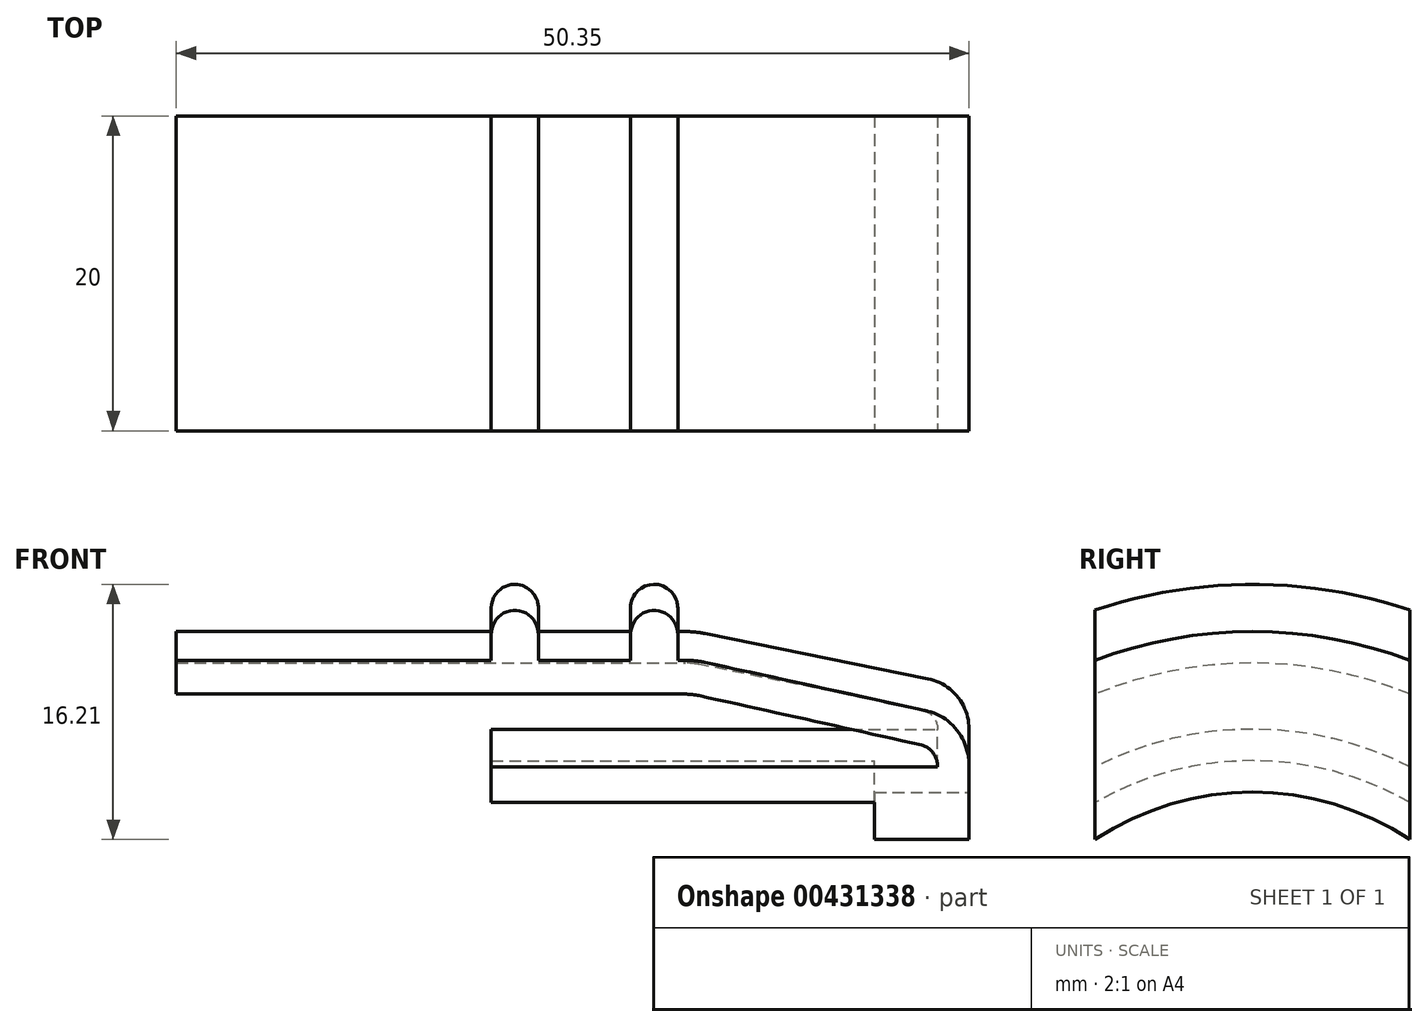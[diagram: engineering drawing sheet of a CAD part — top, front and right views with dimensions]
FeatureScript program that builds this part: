
annotation { "Feature Type Name" : "Feature", "Feature Type Description" : "" }
export const myFeature = defineFeature(function(context is Context, id is Id, definition is map)
    precondition{}
    {
        {
            var Q0;
            Q0=qCreatedBy(makeId("Top.planeOp"),FACE);
            var sketch = newSketch(context, id + "F0", { "sketchPlane" : qUnion([Q0])});
            skLineSegment(sketch, "E0", {"start": v(0, 0) * mm, "end": v(0, 2.22) * mm, "construction": true});
            skLineSegment(sketch, "E1", {"start": v(-1.01, 1.24) * mm, "end": v(-15.58, 4.2) * mm, "construction": true});
            skArc(sketch, "E2", {"start": v(-1.01, 1.24) * mm, "mid": v(-0.29, 0.8) * mm, "end": v(0, 0) * mm});
            skLineSegment(sketch, "E3", {"start": v(-15.58, 4.2) * mm, "end": v(-28.35, 4.2) * mm, "construction": true});
            skArc(sketch, "E4", {"start": v(-15.16, 4.12) * mm, "mid": v(-15.58, 4.18) * mm, "end": v(-16, 4.2) * mm});
            skLineSegment(sketch, "E5", {"start": v(-15.16, 4.12) * mm, "end": v(-1.01, 1.24) * mm});
            skLineSegment(sketch, "E6", {"start": v(-16, 4.2) * mm, "end": v(-28.35, 4.2) * mm});
            skLineSegment(sketch, "E7.0", {"start": v(-16, 6.2) * mm, "end": v(-16.5, 6.2) * mm});
            skArc(sketch, "E7.1", {"start": v(-14.77, 6.08) * mm, "mid": v(-15.38, 6.17) * mm, "end": v(-16, 6.2) * mm});
            skLineSegment(sketch, "E7.2", {"start": v(-14.77, 6.08) * mm, "end": v(-0.62, 3.2) * mm});
            skArc(sketch, "E7.3", {"start": v(-0.62, 3.2) * mm, "mid": v(1.26, 2.07) * mm, "end": v(2, 0) * mm});
            skLineSegment(sketch, "E8", {"start": v(-28.35, 4.2) * mm, "end": v(-28.35, 6.2) * mm, "construction": true});
            skLineSegment(sketch, "E9", {"start": v(2, 0) * mm, "end": v(2, -4) * mm});
            skLineSegment(sketch, "E10", {"start": v(2, -4) * mm, "end": v(-4, -4) * mm});
            skLineSegment(sketch, "E11", {"start": v(-4, -4) * mm, "end": v(-4, -2) * mm});
            skLineSegment(sketch, "E12", {"start": v(-4, -2) * mm, "end": v(-28.35, -2) * mm});
            skLineSegment(sketch, "E13", {"start": v(-28.35, -2) * mm, "end": v(-28.35, 0) * mm});
            skLineSegment(sketch, "E14", {"start": v(-28.35, 0) * mm, "end": v(0, 0) * mm});
            skLineSegment(sketch, "E15", {"start": v(-28.35, 4.2) * mm, "end": v(-28.35, 0) * mm, "construction": true});
            skLineSegment(sketch, "E16", {"start": v(-28.35, 6.2) * mm, "end": v(-28.35, 7.7) * mm});
            skLineSegment(sketch, "E17", {"start": v(-25.35, 7.7) * mm, "end": v(-25.35, 6.2) * mm});
            skLineSegment(sketch, "E18", {"start": v(-19.5, 6.2) * mm, "end": v(-19.5, 7.7) * mm});
            skLineSegment(sketch, "E19", {"start": v(-16.5, 6.2) * mm, "end": v(-16.5, 7.7) * mm});
            skLineSegment(sketch, "E20", {"start": v(-28.35, 7.7) * mm, "end": v(-16.5, 7.7) * mm, "construction": true});
            skArc(sketch, "E21", {"start": v(-25.35, 7.7) * mm, "mid": v(-26.85, 9.2) * mm, "end": v(-28.35, 7.7) * mm});
            skArc(sketch, "E22", {"start": v(-16.5, 7.7) * mm, "mid": v(-18, 9.2) * mm, "end": v(-19.5, 7.7) * mm});
            skLineSegment(sketch, "E23.trimOffspring", {"start": v(-19.5, 6.2) * mm, "end": v(-25.35, 6.2) * mm});
            skLineSegment(sketch, "E24", {"start": v(-28.35, 6.2) * mm, "end": v(-48.35, 6.2) * mm});
            skLineSegment(sketch, "E25", {"start": v(-48.35, 6.2) * mm, "end": v(-48.35, 4.2) * mm});
            skLineSegment(sketch, "E26", {"start": v(-48.35, 4.2) * mm, "end": v(-28.35, 4.2) * mm});
            skSolve(sketch);
        }
        {
            var Q0;
            Q0=qCreatedBy(makeId("Right.planeOp"),FACE);
            var sketch = newSketch(context, id + "F1", { "sketchPlane" : qUnion([Q0])});
            skCircle(sketch, "E27", {"center": v(-22.1, 0) * mm, "radius": 22.1 * mm});
            skSolve(sketch);
        }
        {
            var Q0;
            Q0 = qSketchRegion(id + "F0", true);
            var Q1;
            Q1 = qConstructionFilter(qBodyType(qCreatedBy(id + "F1" ,EDGE), BodyType.WIRE), ConstructionObject.NO);
            sweep(context, id + "F2", {"profiles" : qUnion([Q0]), "path" : qUnion([Q1])});
        }
        {
            var Q0;
            Q0=qCreatedBy(makeId("Top.planeOp"),FACE);
            var sketch = newSketch(context, id + "F3", { "sketchPlane" : qUnion([Q0])});
            skPoint(sketch, "E28", {"position": v(-48.35, 6.2) * mm});
            skPoint(sketch, "E29", {"position": v(-48.35, -50.4) * mm});
            skLineSegment(sketch, "E30", {"start": v(-48.35, 6.2) * mm, "end": v(-48.35, -50.4) * mm});
            skPoint(sketch, "E31", {"position": v(-48.35, -22.1) * mm});
            skPoint(sketch, "E32", {"position": v(-48.35, -12.1) * mm});
            skPoint(sketch, "E33", {"position": v(-48.35, -32.1) * mm});
            skLineSegment(sketch, "E34", {"start": v(-48.35, -22.1) * mm, "end": v(11.65, -22.1) * mm, "construction": true});
            skLineSegment(sketch, "E35", {"start": v(-48.35, -12.1) * mm, "end": v(11.65, -12.1) * mm});
            skLineSegment(sketch, "E36", {"start": v(11.65, -12.1) * mm, "end": v(11.65, -32.1) * mm});
            skLineSegment(sketch, "E37", {"start": v(11.65, -32.1) * mm, "end": v(-48.35, -32.1) * mm});
            skSolve(sketch);
        }
        {
            var Q0;
            Q0 = qSketchRegion(id + "F3", true);
            extrude(context, id + "F4", {"entities" : qUnion([Q0]), "operationType" : NewBodyOperationType.INTERSECT, "endBound" : BoundingType.THROUGH_ALL, "depth" : 25 * mm});
        }
    });
